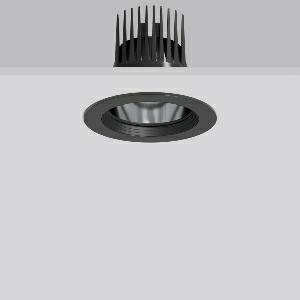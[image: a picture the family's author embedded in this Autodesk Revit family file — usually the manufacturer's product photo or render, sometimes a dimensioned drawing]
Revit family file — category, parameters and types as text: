
# Revit family: heledon_maxi_e_901764_003_3_76_1482
name_source: partatom
category: Lighting Fixtures
units: mm (PartAtom-declared; Revit-internal decimal feet)

## family parameters
Cut with Voids When Loaded = No
Host = Face
Light Source = No
Part Type = Normal
Room Calculation Point = No
Round Connector Dimension = Use Diameter
Shared = No

## types (1)
- HELEDON maxi E (1 x LED Modul 935, 4350 lm, 3500)
    Apparent Load = 35 VA
    Approval mark = CE
    CIE Flux Codes = 100 100 100 100 100
    Color Rendering = 92
    Color Temperature = 3500
    Default Elevation = 1800 mm
    Description = Series: HELEDON maxi
Round recessed downlight. Housing: die-cast aluminium, powder-coated. Black plastic ring and recessed LED to prevent glare from the side. Optical assembly with reflector made of MIRO-Silver with 98% total light reflection for outstanding efficiency - can be changed without tools. Best colour rendering index Ra>90. Suitable for Recessed ceiling mounting. Installation without tools thanks to spring fastening system. Including separate LED converter with connecting cable 600 mm.High quality converter without flickering and stroboscopic effect. Through-wiring box (5 pole) available as accessory. The following accessories can be mounted without use of tools: interchangeable lenses, decorative glasses, honeycomb louvre, clear and frosted diffusers, white interchangeable plastic ring. 
Colour: deep black, matt (RAL 9005)
Diameter: 162 mm
Height: 3 mm
Cut-out diameter: 152 mm
Recess height: 200 mm
Luminaire: recess height: 135 mm
Lamp: LED
Socket: without socket
Colour temperature: 3500K
Colour rendering index (CRI): 92
System power: 35 W
Rated luminous flux: 4350 lm
Luminous efficiency: 124 lm/W
Control gear: Converter, dimmable, DALI
Protection class: II
Type of protection: IP 20
    Height = 0 mm  [stored 0 ft]
    Lamp = 1 x LED Modul 935
    Lamp Light Flux = 4350 lm
    Lamp count = 1
    Length = 162 mm
    Lifetime = 50000 h
    Luminous efficacy = 124 lm/W
    Manufacturer = RZB
    ModVariant = No
    Model = 901764.003.3.76
    Mounting Place = Ceiling
    Mounting Type = Recessed
    Number of Poles = 1
    OnlyDefault = Yes
    Power Factor = 1
    Product Name = HELEDON maxi E
    Product group = Recessed downlights
    ProductGroupID = 402
    Protection Class = Protection class II
    Protection Degree = IP 20
    RLX_Detail_Level = 1
    RLX_Emergency_Light_Flux = 0 lm
    RLX_Emergency_Type = 0
    RLX_Emergency_Type_DB = No
    RlxData = <blob elided: 121925 chars, md5=461f7481>
    Socket = socket
    Standby Power = 0 W
    System Light Flux = 4350 lm
    System Power = 35 W
    Type Comments = Product without accessories
    Type Image = 901662.003.jpg
    URL = http://relux.com
    VarID = ---
    Voltage = 230 V
    Voltage Range = 220-240 V
    Weight = 0.00 kg
    Width = 0 mm  [stored 0 ft]

note: [stored X ft] marks values corroborated as IEEE doubles in the binary element streams (Revit-internal decimal feet)

## geometry (parser evidence)
native form markers: Blend x4, Sweep x11
no freeform markers — native parametric forms only
